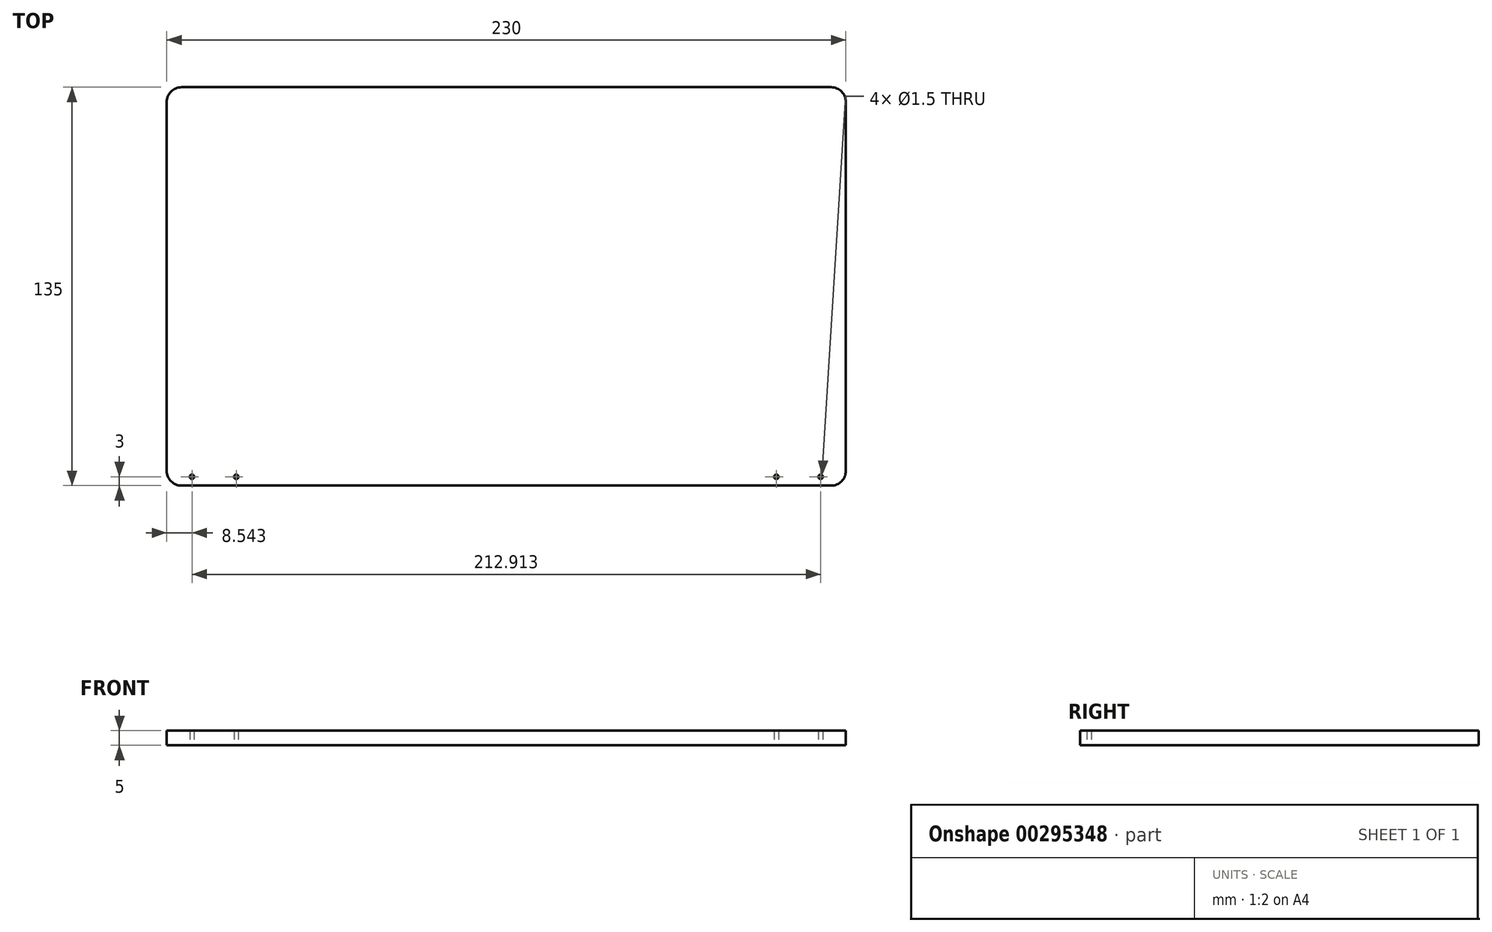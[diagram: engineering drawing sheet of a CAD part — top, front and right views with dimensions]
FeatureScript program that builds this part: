
annotation { "Feature Type Name" : "Feature", "Feature Type Description" : "" }
export const myFeature = defineFeature(function(context is Context, id is Id, definition is map)
    precondition{}
    {
        {
            var Q0;
            Q0=qCreatedBy(makeId("Top.planeOp"),FACE);
            var sketch = newSketch(context, id + "F0", { "sketchPlane" : qUnion([Q0])});
            skLineSegment(sketch, "E0.bottom", {"start": v(110, -67.5) * mm, "end": v(-110, -67.5) * mm});
            skLineSegment(sketch, "E0.top", {"start": v(110, 67.5) * mm, "end": v(-110, 67.5) * mm});
            skLineSegment(sketch, "E0.left", {"start": v(115, -62.5) * mm, "end": v(115, 62.5) * mm});
            skLineSegment(sketch, "E0.right", {"start": v(-115, -62.5) * mm, "end": v(-115, 62.5) * mm});
            skPoint(sketch, "E0.middle", {"position": v(0, 0) * mm});
            skCircle(sketch, "E1", {"center": v(-106.46, -64.5) * mm, "radius": 0.75 * mm});
            skCircle(sketch, "E2", {"center": v(-91.46, -64.5) * mm, "radius": 0.75 * mm});
            skCircle(sketch, "E3", {"center": v(106.46, -64.5) * mm, "radius": 0.75 * mm});
            skCircle(sketch, "E4", {"center": v(91.46, -64.5) * mm, "radius": 0.75 * mm});
            skPoint(sketch, "E5.visualSharp", {"position": v(-115, 67.5) * mm});
            skArc(sketch, "E5.filletArc", {"start": v(-110, 67.5) * mm, "mid": v(-113.54, 66.04) * mm, "end": v(-115, 62.5) * mm});
            skPoint(sketch, "E6.visualSharp", {"position": v(115, 67.5) * mm});
            skArc(sketch, "E6.filletArc", {"start": v(115, 62.5) * mm, "mid": v(113.54, 66.04) * mm, "end": v(110, 67.5) * mm});
            skPoint(sketch, "E7.visualSharp", {"position": v(115, -67.5) * mm});
            skArc(sketch, "E7.filletArc", {"start": v(110, -67.5) * mm, "mid": v(113.54, -66.04) * mm, "end": v(115, -62.5) * mm});
            skPoint(sketch, "E8.visualSharp", {"position": v(-115, -67.5) * mm});
            skArc(sketch, "E8.filletArc", {"start": v(-115, -62.5) * mm, "mid": v(-113.54, -66.04) * mm, "end": v(-110, -67.5) * mm});
            skSolve(sketch);
        }
        {
            var Q0;
            Q0=makeQuery(id+"F0.imprint","IMPRINT",FACE,{"disambiguationData":[TD([[makeQuery(id+"F0.imprint","IMPRINT",EDGE,{"derivedFrom":sQuery(id+"F0.wireOp",EDGE,"E0.bottom")}),-1.0]])]});
            extrude(context, id + "F1", {"entities" : qUnion([Q0]), "depth" : 5 * mm});
        }
    });
